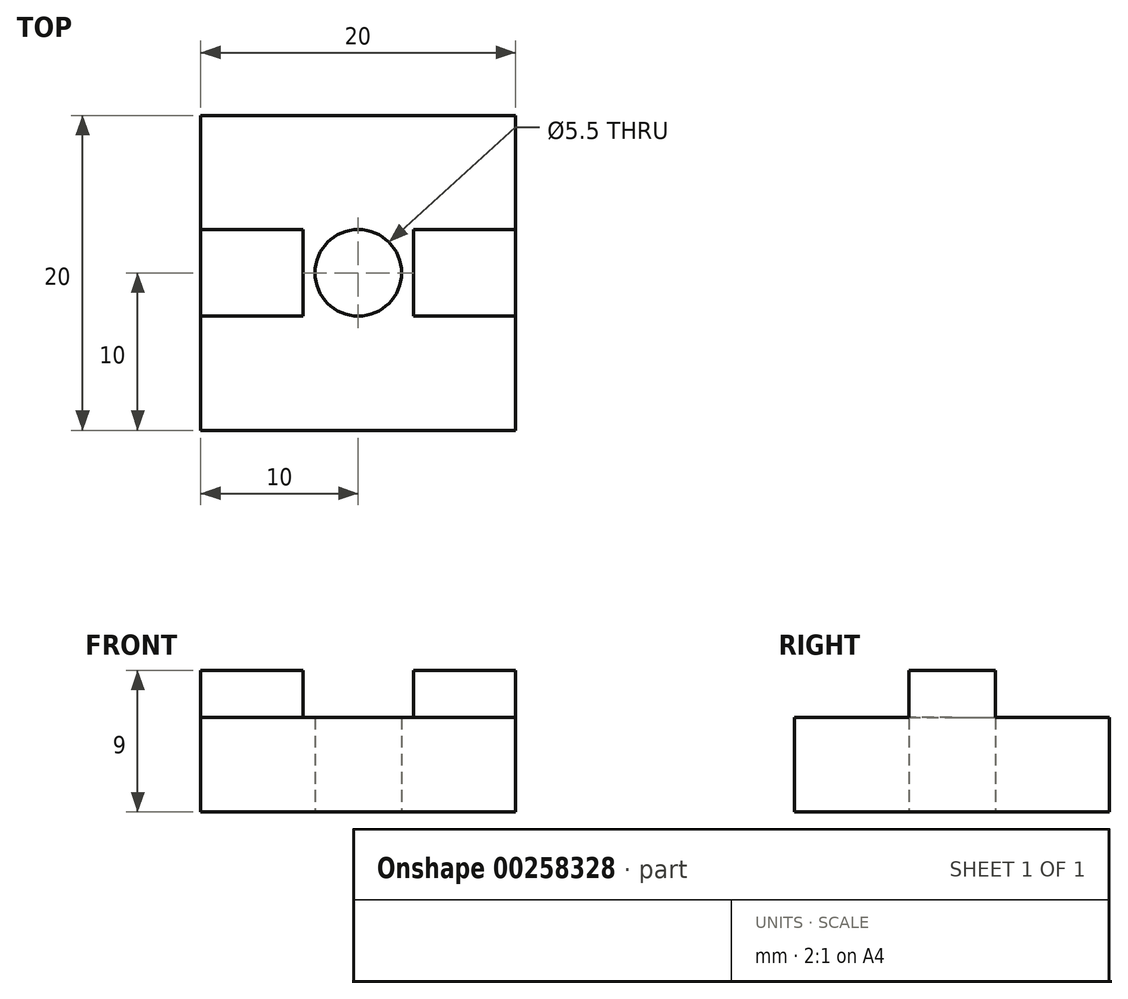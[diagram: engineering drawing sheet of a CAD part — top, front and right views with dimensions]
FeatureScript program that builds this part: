
annotation { "Feature Type Name" : "Feature", "Feature Type Description" : "" }
export const myFeature = defineFeature(function(context is Context, id is Id, definition is map)
    precondition{}
    {
        {
            var Q0;
            Q0=qCreatedBy(makeId("Top.planeOp"),FACE);
            var sketch = newSketch(context, id + "F0", { "sketchPlane" : qUnion([Q0])});
            skLineSegment(sketch, "E0.bottom", {"start": v(10, -10) * mm, "end": v(-10, -10) * mm});
            skLineSegment(sketch, "E0.top", {"start": v(10, 10) * mm, "end": v(-10, 10) * mm});
            skLineSegment(sketch, "E0.left", {"start": v(10, -10) * mm, "end": v(10, 10) * mm});
            skLineSegment(sketch, "E0.right", {"start": v(-10, -10) * mm, "end": v(-10, 10) * mm});
            skPoint(sketch, "E0.middle", {"position": v(0, 0) * mm});
            skSolve(sketch);
        }
        {
            var Q0;
            Q0 = qSketchRegion(id + "F0", true);
            extrude(context, id + "F1", {"entities" : qUnion([Q0]), "depth" : 6 * mm, "offsetDistance" : 25 * mm});
        }
        {
            var Q0;
            Q0=makeQuery(id+"F1.opExtrude","CAP_FACE",FACE,{"disambiguationData":[OSD([sQuery(id+"F0.wireOp",EDGE,"E0.bottom"),sQuery(id+"F0.wireOp",EDGE,"E0.top"),sQuery(id+"F0.wireOp",EDGE,"E0.left"),sQuery(id+"F0.wireOp",EDGE,"E0.right"),sQuery(id+"F0.wireOp",EDGE,"YxrAET8V-at9v-hmdi-ILWs-7U4ft1vcAltx")])],"isStart":false});
            var sketch = newSketch(context, id + "F2", { "sketchPlane" : qUnion([Q0])});
            skLineSegment(sketch, "E1.bottom", {"start": v(10, -2.75) * mm, "end": v(3.5, -2.75) * mm});
            skLineSegment(sketch, "E1.top", {"start": v(10, 2.75) * mm, "end": v(3.5, 2.75) * mm});
            skLineSegment(sketch, "E1.left", {"start": v(10, -2.75) * mm, "end": v(10, 2.75) * mm});
            skLineSegment(sketch, "E1.right", {"start": v(-10, -2.75) * mm, "end": v(-10, 2.75) * mm});
            skPoint(sketch, "E1.middle", {"position": v(0, 0) * mm});
            skLineSegment(sketch, "E2.left", {"start": v(3.5, -2.75) * mm, "end": v(3.5, 2.75) * mm});
            skLineSegment(sketch, "E2.right", {"start": v(-3.5, -2.75) * mm, "end": v(-3.5, 2.75) * mm});
            skLineSegment(sketch, "E3.trimOffspring", {"start": v(-3.5, 2.75) * mm, "end": v(-10, 2.75) * mm});
            skLineSegment(sketch, "E4.trimOffspring", {"start": v(-3.5, -2.75) * mm, "end": v(-10, -2.75) * mm});
            skSolve(sketch);
        }
        {
            var Q0;
            Q0 = qSketchRegion(id + "F2", true);
            extrude(context, id + "F3", {"entities" : qUnion([Q0]), "operationType" : NewBodyOperationType.ADD, "depth" : 3 * mm, "offsetDistance" : 25 * mm});
        }
        {
            var Q0;
            Q0=makeQuery(id+"F1.opExtrude","CAP_FACE",FACE,{"disambiguationData":[OSD([sQuery(id+"F0.wireOp",EDGE,"E0.bottom"),sQuery(id+"F0.wireOp",EDGE,"E0.top"),sQuery(id+"F0.wireOp",EDGE,"E0.left"),sQuery(id+"F0.wireOp",EDGE,"E0.right")])],"isStart":true});
            var sketch = newSketch(context, id + "F4", { "sketchPlane" : qUnion([Q0])});
            skCircle(sketch, "E5", {"center": v(0, 0) * mm, "radius": 2.75 * mm});
            skSolve(sketch);
        }
        {
            var Q0;
            Q0 = qSketchRegion(id + "F4", true);
            extrude(context, id + "F5", {"entities" : qUnion([Q0]), "operationType" : NewBodyOperationType.REMOVE, "endBound" : BoundingType.THROUGH_ALL, "oppositeDirection" : true, "depth" : 25 * mm, "offsetDistance" : 25 * mm});
        }
    });
